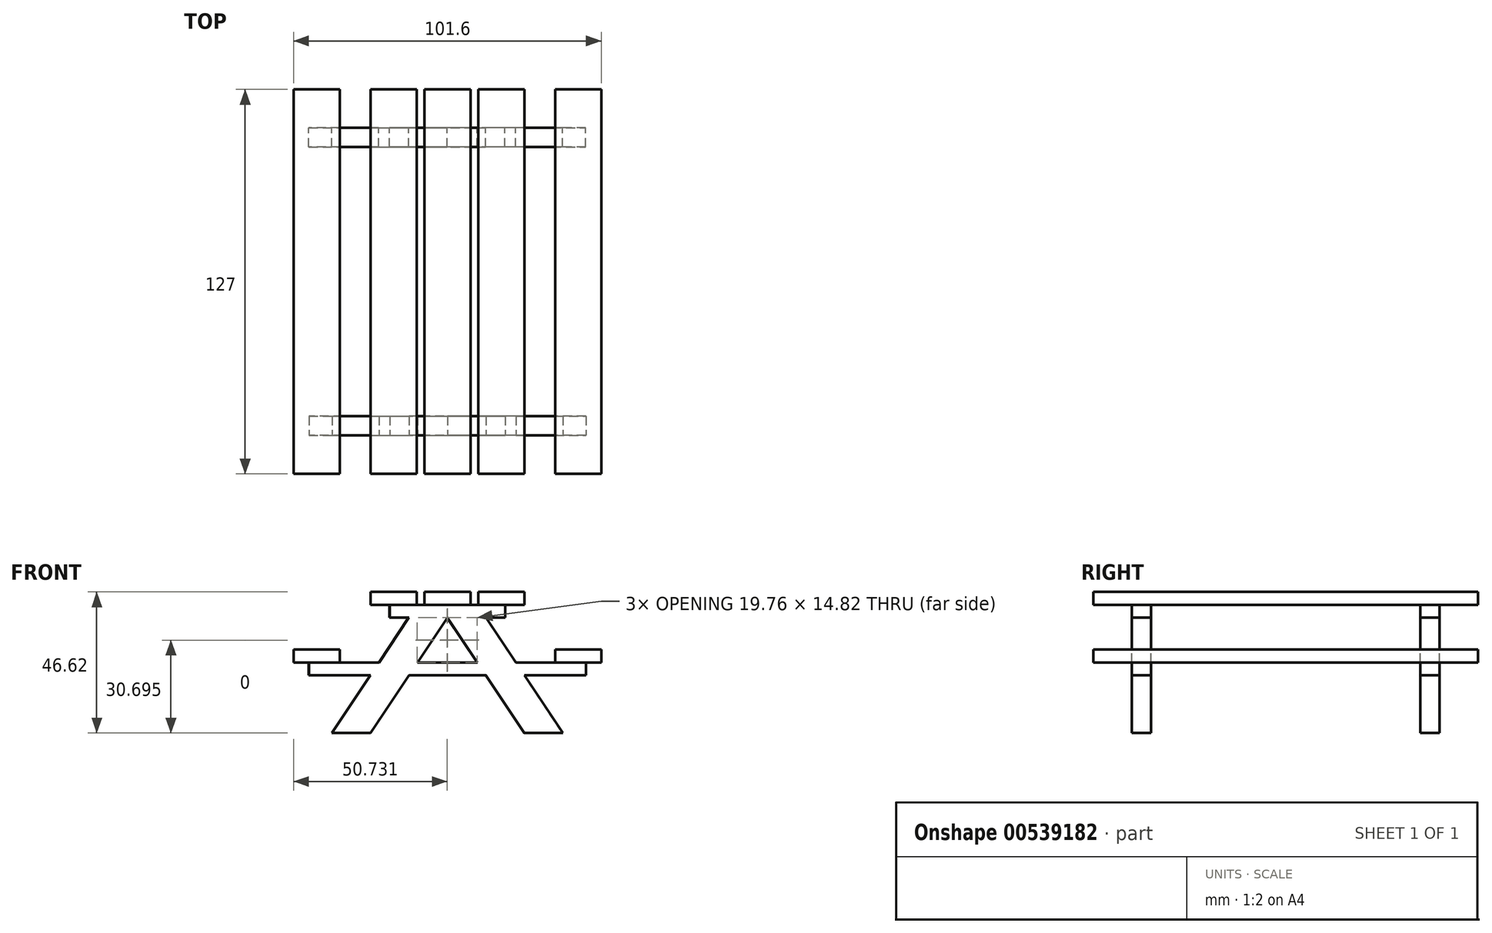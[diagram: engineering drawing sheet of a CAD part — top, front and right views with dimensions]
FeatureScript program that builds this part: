
annotation { "Feature Type Name" : "Feature", "Feature Type Description" : "" }
export const myFeature = defineFeature(function(context is Context, id is Id, definition is map)
    precondition{}
    {
        {
            var Q0;
            Q0=qCreatedBy(makeId("Top.planeOp"),FACE);
            var sketch = newSketch(context, id + "F0", { "sketchPlane" : qUnion([Q0])});
            skLineSegment(sketch, "E0", {"start": v(-25.4, 63.5) * mm, "end": v(-25.4, -63.5) * mm});
            skLineSegment(sketch, "E1", {"start": v(-25.4, -63.5) * mm, "end": v(-10.16, -63.5) * mm});
            skLineSegment(sketch, "E2", {"start": v(25.4, -63.5) * mm, "end": v(25.4, 63.5) * mm});
            skLineSegment(sketch, "E3", {"start": v(-25.4, 63.5) * mm, "end": v(-10.16, 63.5) * mm});
            skLineSegment(sketch, "E4", {"start": v(-10.16, 63.5) * mm, "end": v(-10.16, -63.5) * mm});
            skLineSegment(sketch, "E5", {"start": v(25.4, 63.5) * mm, "end": v(10.16, 63.5) * mm});
            skLineSegment(sketch, "E6", {"start": v(10.16, 63.5) * mm, "end": v(10.16, -63.5) * mm});
            skLineSegment(sketch, "E7", {"start": v(7.62, 63.5) * mm, "end": v(-7.62, 63.5) * mm});
            skLineSegment(sketch, "E8", {"start": v(-7.62, 63.5) * mm, "end": v(-7.62, -63.5) * mm});
            skLineSegment(sketch, "E9", {"start": v(7.62, 63.5) * mm, "end": v(7.62, -63.5) * mm});
            skLineSegment(sketch, "E10.trimOffspring", {"start": v(10.16, -63.5) * mm, "end": v(25.4, -63.5) * mm});
            skLineSegment(sketch, "E11.trimOffspring", {"start": v(-7.62, -63.5) * mm, "end": v(7.62, -63.5) * mm});
            skSolve(sketch);
        }
        {
            var Q0;
            Q0 = qSketchRegion(id + "F0", true);
            extrude(context, id + "F1", {"entities" : qUnion([Q0]), "depth" : 4.23 * mm, "offsetDistance" : 25.4 * mm});
        }
        {
            var Q0;
            Q0=makeQuery(id+"F1.opExtrude","SWEPT_FACE",FACE,{"disambiguationData":[OSD([sQuery(id+"F0.wireOp",EDGE,"E1")])]});
            cPlane(context, id + "F2", {"entities" : qUnion([Q0]), "cplaneType" : CPlaneType.OFFSET, "offset" : 12.7 * mm, "oppositeDirection" : true, "width" : 152.4 * mm, "height" : 152.4 * mm});
        }
        {
            var Q0;
            Q0=qCreatedBy(id+"F2.planeOp",FACE);
            var sketch = newSketch(context, id + "F3", { "sketchPlane" : qUnion([Q0])});
            skLineSegment(sketch, "E12", {"start": v(-19.05, 0) * mm, "end": v(-19.05, -4.23) * mm});
            skLineSegment(sketch, "E13", {"start": v(-19.05, -4.23) * mm, "end": v(-12.7, -4.23) * mm});
            skLineSegment(sketch, "E14", {"start": v(19.05, -4.23) * mm, "end": v(19.05, 0) * mm});
            skLineSegment(sketch, "E15", {"start": v(-19.05, 0) * mm, "end": v(19.05, 0) * mm});
            skPoint(sketch, "E16.endSnap0", {"position": v(0, -4.23) * mm});
            skLineSegment(sketch, "E17", {"start": v(25.4, -42.33) * mm, "end": v(12.7, -23.28) * mm});
            skLineSegment(sketch, "E18", {"start": v(-25.4, -42.33) * mm, "end": v(-12.7, -23.28) * mm});
            skLineSegment(sketch, "E19", {"start": v(25.4, -42.33) * mm, "end": v(38.1, -42.33) * mm});
            skLineSegment(sketch, "E20", {"start": v(38.1, -42.33) * mm, "end": v(25.4, -23.28) * mm});
            skLineSegment(sketch, "E21", {"start": v(-25.4, -42.33) * mm, "end": v(-38.1, -42.33) * mm});
            skLineSegment(sketch, "E22", {"start": v(-38.1, -42.33) * mm, "end": v(-25.4, -23.28) * mm});
            skPoint(sketch, "E23.endSnap0", {"position": v(-12.7, -23.28) * mm});
            skPoint(sketch, "E24.endSnap0", {"position": v(25.4, -23.28) * mm});
            skLineSegment(sketch, "E25", {"start": v(38.1, -23.28) * mm, "end": v(25.4, -23.28) * mm});
            skPoint(sketch, "E25.endSnap0", {"position": v(-25.4, -23.28) * mm});
            skLineSegment(sketch, "E26", {"start": v(-38.1, -23.28) * mm, "end": v(-45.72, -23.28) * mm});
            skLineSegment(sketch, "E27", {"start": v(38.1, -23.28) * mm, "end": v(45.72, -23.28) * mm});
            skLineSegment(sketch, "E28", {"start": v(-45.72, -23.28) * mm, "end": v(-45.72, -19.05) * mm});
            skLineSegment(sketch, "E29", {"start": v(-45.72, -19.05) * mm, "end": v(-22.58, -19.05) * mm});
            skLineSegment(sketch, "E30", {"start": v(45.72, -23.28) * mm, "end": v(45.72, -19.05) * mm});
            skLineSegment(sketch, "E31.trimOffspring", {"start": v(22.58, -19.05) * mm, "end": v(45.72, -19.05) * mm});
            skLineSegment(sketch, "E32.trimOffspring", {"start": v(12.7, -23.28) * mm, "end": v(-12.7, -23.28) * mm});
            skLineSegment(sketch, "E33.trimOffspring", {"start": v(9.88, -19.05) * mm, "end": v(0, -4.23) * mm});
            skLineSegment(sketch, "E34.trimOffspring", {"start": v(22.58, -19.05) * mm, "end": v(12.7, -4.23) * mm});
            skLineSegment(sketch, "E35.trimOffspring", {"start": v(-9.88, -19.05) * mm, "end": v(0, -4.23) * mm});
            skLineSegment(sketch, "E36.trimOffspring", {"start": v(-9.88, -19.05) * mm, "end": v(9.88, -19.05) * mm});
            skLineSegment(sketch, "E37.trimOffspring", {"start": v(-25.4, -23.28) * mm, "end": v(-38.1, -23.28) * mm});
            skLineSegment(sketch, "E38.trimOffspring", {"start": v(-22.58, -19.05) * mm, "end": v(-12.7, -4.23) * mm});
            skLineSegment(sketch, "E39.trimOffspring", {"start": v(12.7, -4.23) * mm, "end": v(19.05, -4.23) * mm});
            skSolve(sketch);
        }
        {
            var Q0;
            Q0 = qSketchRegion(id + "F3", true);
            extrude(context, id + "F4", {"entities" : qUnion([Q0]), "oppositeDirection" : true, "depth" : 6.35 * mm, "offsetDistance" : 25.4 * mm});
        }
        {
            var Q0;
            Q0=makeQuery(id+"F1.opExtrude","SWEPT_FACE",FACE,{"disambiguationData":[OSD([sQuery(id+"F0.wireOp",EDGE,"E3")])]});
            cPlane(context, id + "F5", {"entities" : qUnion([Q0]), "cplaneType" : CPlaneType.OFFSET, "offset" : 12.7 * mm, "oppositeDirection" : true, "width" : 152.4 * mm, "height" : 152.4 * mm});
        }
        {
            var Q0;
            Q0=qCreatedBy(id+"F5.planeOp",FACE);
            var sketch = newSketch(context, id + "F6", { "sketchPlane" : qUnion([Q0])});
            skLineSegment(sketch, "E40", {"start": v(-18.98, -0.05) * mm, "end": v(-18.98, -4.29) * mm});
            skLineSegment(sketch, "E41", {"start": v(-18.98, -4.29) * mm, "end": v(-12.63, -4.29) * mm});
            skLineSegment(sketch, "E42", {"start": v(19.12, -4.29) * mm, "end": v(19.12, -0.05) * mm});
            skLineSegment(sketch, "E43", {"start": v(-18.98, -0.05) * mm, "end": v(19.12, -0.05) * mm});
            skPoint(sketch, "E44.endSnap0", {"position": v(0.07, -4.29) * mm});
            skLineSegment(sketch, "E45", {"start": v(25.47, -42.39) * mm, "end": v(12.77, -23.34) * mm});
            skLineSegment(sketch, "E46", {"start": v(-25.33, -42.39) * mm, "end": v(-12.63, -23.34) * mm});
            skLineSegment(sketch, "E47", {"start": v(25.47, -42.39) * mm, "end": v(38.17, -42.39) * mm});
            skLineSegment(sketch, "E48", {"start": v(38.17, -42.39) * mm, "end": v(25.47, -23.34) * mm});
            skLineSegment(sketch, "E49", {"start": v(-25.33, -42.39) * mm, "end": v(-38.03, -42.39) * mm});
            skLineSegment(sketch, "E50", {"start": v(-38.03, -42.39) * mm, "end": v(-25.33, -23.34) * mm});
            skPoint(sketch, "E51.endSnap0", {"position": v(-12.63, -23.34) * mm});
            skPoint(sketch, "E52.endSnap0", {"position": v(25.47, -23.34) * mm});
            skLineSegment(sketch, "E53", {"start": v(38.35, -23.34) * mm, "end": v(25.47, -23.34) * mm});
            skPoint(sketch, "E53.endSnap0", {"position": v(-25.33, -23.34) * mm});
            skLineSegment(sketch, "E54", {"start": v(-37.85, -23.34) * mm, "end": v(-45.65, -23.34) * mm});
            skLineSegment(sketch, "E55", {"start": v(38.35, -23.34) * mm, "end": v(45.79, -23.34) * mm});
            skLineSegment(sketch, "E56", {"start": v(-45.65, -23.34) * mm, "end": v(-45.65, -19.1) * mm});
            skLineSegment(sketch, "E57", {"start": v(-45.65, -19.1) * mm, "end": v(-22.5, -19.1) * mm});
            skLineSegment(sketch, "E58", {"start": v(45.79, -23.34) * mm, "end": v(45.79, -19.1) * mm});
            skLineSegment(sketch, "E59.trimOffspring", {"start": v(22.65, -19.1) * mm, "end": v(45.79, -19.1) * mm});
            skLineSegment(sketch, "E60.trimOffspring", {"start": v(12.77, -23.34) * mm, "end": v(-12.63, -23.34) * mm});
            skLineSegment(sketch, "E61.trimOffspring", {"start": v(9.95, -19.1) * mm, "end": v(0.07, -4.29) * mm});
            skLineSegment(sketch, "E62.trimOffspring", {"start": v(22.65, -19.1) * mm, "end": v(12.77, -4.29) * mm});
            skLineSegment(sketch, "E63.trimOffspring", {"start": v(-9.8, -19.1) * mm, "end": v(0.07, -4.29) * mm});
            skLineSegment(sketch, "E64.trimOffspring", {"start": v(-9.8, -19.1) * mm, "end": v(9.95, -19.1) * mm});
            skLineSegment(sketch, "E65.trimOffspring", {"start": v(-25.33, -23.34) * mm, "end": v(-37.85, -23.34) * mm});
            skLineSegment(sketch, "E66.trimOffspring", {"start": v(-22.5, -19.1) * mm, "end": v(-12.63, -4.29) * mm});
            skLineSegment(sketch, "E67.trimOffspring", {"start": v(12.77, -4.29) * mm, "end": v(19.12, -4.29) * mm});
            skSolve(sketch);
        }
        {
            var Q0;
            Q0=makeQuery(id+"F6.imprint","IMPRINT",FACE,{"disambiguationData":[TD([[makeQuery(id+"F6.imprint","IMPRINT",EDGE,{"derivedFrom":sQuery(id+"F6.wireOp",EDGE,"E40")}),1.0]])]});
            extrude(context, id + "F7", {"entities" : qUnion([Q0]), "oppositeDirection" : true, "depth" : 6.35 * mm, "offsetDistance" : 25.4 * mm});
        }
        {
            var Q0;
            Q0=makeQuery(id+"F1.opExtrude","SWEPT_FACE",FACE,{"disambiguationData":[OSD([sQuery(id+"F0.wireOp",EDGE,"E3")])]});
            cPlane(context, id + "F8", {"entities" : qUnion([Q0]), "cplaneType" : CPlaneType.OFFSET, "offset" : 0 * mm, "width" : 152.4 * mm, "height" : 152.4 * mm});
        }
        {
            var Q0;
            Q0=qCreatedBy(id+"F8.planeOp",FACE);
            var sketch = newSketch(context, id + "F9", { "sketchPlane" : qUnion([Q0])});
            skLineSegment(sketch, "E68", {"start": v(-78.1, 26.44) * mm, "end": v(-78.1, 30.67) * mm});
            skLineSegment(sketch, "E69", {"start": v(13.33, 26.44) * mm, "end": v(13.33, 30.67) * mm});
            skLineSegment(sketch, "E70", {"start": v(35.56, -19.05) * mm, "end": v(50.8, -19.05) * mm});
            skLineSegment(sketch, "E71", {"start": v(50.8, -19.05) * mm, "end": v(50.8, -14.82) * mm});
            skLineSegment(sketch, "E72", {"start": v(50.8, -14.82) * mm, "end": v(35.56, -14.82) * mm});
            skLineSegment(sketch, "E73", {"start": v(-35.56, -19.05) * mm, "end": v(-50.8, -19.05) * mm});
            skLineSegment(sketch, "E74", {"start": v(-50.8, -19.05) * mm, "end": v(-50.8, -14.82) * mm});
            skLineSegment(sketch, "E75", {"start": v(-50.8, -14.82) * mm, "end": v(-35.56, -14.82) * mm});
            skLineSegment(sketch, "E76", {"start": v(-35.56, -14.82) * mm, "end": v(-35.56, -19.05) * mm});
            skLineSegment(sketch, "E77", {"start": v(35.56, -14.82) * mm, "end": v(35.56, -19.05) * mm});
            skSolve(sketch);
        }
        {
            var Q0;
            Q0 = qSketchRegion(id + "F9", true);
            extrude(context, id + "F10", {"entities" : qUnion([Q0]), "operationType" : NewBodyOperationType.ADD, "oppositeDirection" : true, "depth" : 127 * mm, "offsetDistance" : 25.4 * mm});
        }
    });
